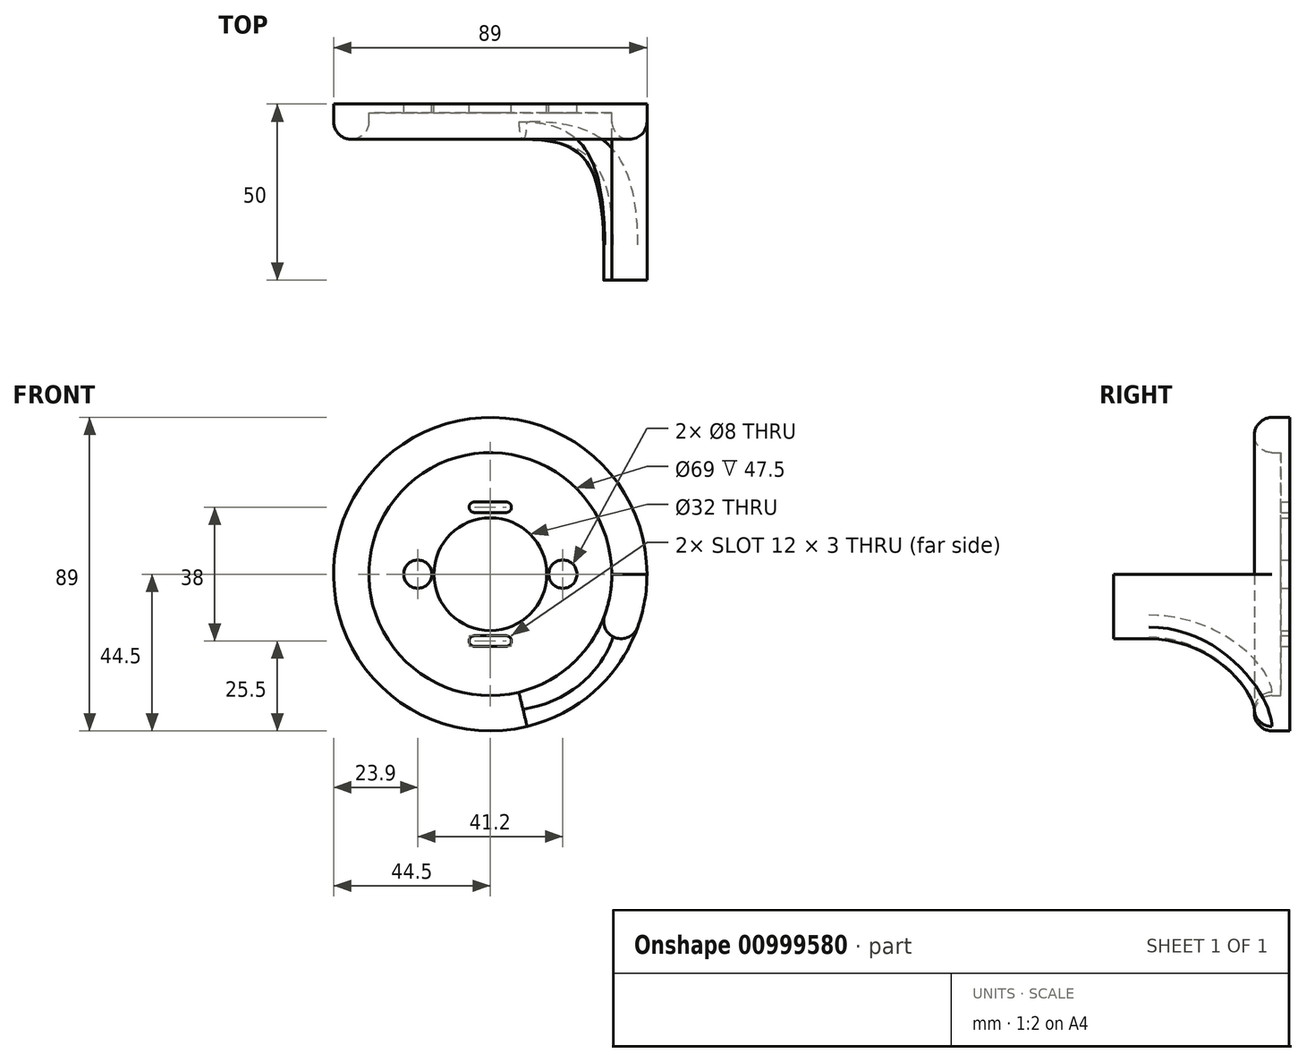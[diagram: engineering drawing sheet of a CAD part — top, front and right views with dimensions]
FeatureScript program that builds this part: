
annotation { "Feature Type Name" : "Feature", "Feature Type Description" : "" }
export const myFeature = defineFeature(function(context is Context, id is Id, definition is map)
    precondition{}
    {
        {
            var Q0;
            Q0=qCreatedBy(makeId("Front.planeOp"),FACE);
            var sketch = newSketch(context, id + "F0", { "sketchPlane" : qUnion([Q0])});
            skCircle(sketch, "E0", {"center": v(0, 0) * mm, "radius": 34.5 * mm});
            skCircle(sketch, "E1", {"center": v(0, 0) * mm, "radius": 44.5 * mm});
            skLineSegment(sketch, "E2", {"start": v(30.74, -15.66) * mm, "end": v(39.65, -20.2) * mm});
            skLineSegment(sketch, "E3", {"start": v(34.5, 0) * mm, "end": v(44.5, 0) * mm});
            skCircle(sketch, "E4", {"center": v(-20.6, 0) * mm, "radius": 4 * mm});
            skCircle(sketch, "E5.MirrorC", {"center": v(20.6, 0) * mm, "radius": 4 * mm});
            skCircle(sketch, "E6", {"center": v(0, 0) * mm, "radius": 16 * mm});
            skArc(sketch, "E7", {"start": v(4.5, 17.5) * mm, "mid": v(6, 19) * mm, "end": v(4.5, 20.5) * mm});
            skLineSegment(sketch, "E8", {"start": v(4.5, 20.5) * mm, "end": v(0, 20.5) * mm});
            skLineSegment(sketch, "E9", {"start": v(4.5, 17.5) * mm, "end": v(0, 17.5) * mm});
            skLineSegment(sketch, "E10.MirrorCS", {"start": v(-4.5, 17.5) * mm, "end": v(0, 17.5) * mm});
            skArc(sketch, "E11.MirrorCS", {"start": v(-4.5, 17.5) * mm, "mid": v(-6, 19) * mm, "end": v(-4.5, 20.5) * mm});
            skLineSegment(sketch, "E12.MirrorCS", {"start": v(-4.5, 20.5) * mm, "end": v(0, 20.5) * mm});
            skLineSegment(sketch, "E13.MirrorCS", {"start": v(-4.5, -17.5) * mm, "end": v(0, -17.5) * mm});
            skArc(sketch, "E14.MirrorCS", {"start": v(4.5, -17.5) * mm, "mid": v(6, -19) * mm, "end": v(4.5, -20.5) * mm});
            skArc(sketch, "E15.MirrorCS", {"start": v(-4.5, -17.5) * mm, "mid": v(-6, -19) * mm, "end": v(-4.5, -20.5) * mm});
            skLineSegment(sketch, "E16.MirrorCS", {"start": v(4.5, -17.5) * mm, "end": v(0, -17.5) * mm});
            skLineSegment(sketch, "E17.MirrorCS", {"start": v(-4.5, -20.5) * mm, "end": v(0, -20.5) * mm});
            skLineSegment(sketch, "E18.MirrorCS", {"start": v(4.5, -20.5) * mm, "end": v(0, -20.5) * mm});
            skSolve(sketch);
        }
        {
            var Q0;
            Q0=makeQuery(id+"F0.imprint","IMPRINT",FACE,{"disambiguationData":[TD([[makeQuery(id+"F0.imprint","IMPRINT",EDGE,{"derivedFrom":sQuery(id+"F0.wireOp",EDGE,"E0")}),-1.0]])]});
            extrude(context, id + "F1", {"entities" : qUnion([Q0]), "depth" : 10 * mm, "offsetDistance" : 25 * mm});
        }
        {
            var Q0;
            {var subQ0=sQuery(id+"F0.wireOp",EDGE,"E2");Q0=makeQuery(id+"F0.imprint","IMPRINT",FACE,{"disambiguationData":[TD([[makeQuery(id+"F0.imprint","IMPRINT",EDGE,{"derivedFrom":subQ0}),1.0]])]});}
            extrude(context, id + "F2", {"entities" : qUnion([Q0]), "operationType" : NewBodyOperationType.ADD, "depth" : 50 * mm, "offsetDistance" : 25 * mm});
        }
        {
            var Q0;
            Q0=makeQuery(id+"F2.boolean.opBoolean","INTERSECT",EDGE,{"derivedFrom":[makeQuery(id+"F1.opExtrude","CAP_FACE",FACE,{"disambiguationData":[OSD([sQuery(id+"F0.wireOp",EDGE,"E0"),sQuery(id+"F0.wireOp",EDGE,"E1")])],"isStart":false}),makeQuery(id+"F2.opExtrude","SWEPT_FACE",FACE,{"disambiguationData":[OSD([sQuery(id+"F0.wireOp",EDGE,"E2")])]})]});
            fillet(context, id + "F3", {"entities" : qUnion([Q0]), "radius" : 30 * mm, "tangentPropagation" : true, "allowEdgeOverflow" : false});
        }
        {
            var Q0;
            {var subQ0=sQuery(id+"F0.wireOp",EDGE,"E0");var subQ1=makeQuery(id+"F0.imprint","INTERSECT",VERTEX,{"derivedFrom":[subQ0,sQuery(id+"F0.wireOp",EDGE,"E2")]});Q0=makeQuery(id+"F0.imprint","IMPRINT",FACE,{"disambiguationData":[TD([[makeQuery(id+"F0.imprint","IMPRINT",EDGE,{"disambiguationData":[TD([[subQ1,1.0]])],"derivedFrom":subQ0}),1.0]])]});}
            extrude(context, id + "F4", {"entities" : qUnion([Q0]), "operationType" : NewBodyOperationType.ADD, "depth" : 2.5 * mm, "offsetDistance" : 25 * mm});
        }
        {
            var Q0;
            Q0=makeQuery(id+"F1.opExtrude","CAP_EDGE",EDGE,{"disambiguationData":[OSD([sQuery(id+"F0.wireOp",EDGE,"E0")])],"isStart":false});
            var Q1;
            Q1=makeQuery(id+"F1.opExtrude","CAP_EDGE",EDGE,{"disambiguationData":[OSD([sQuery(id+"F0.wireOp",EDGE,"E1")])],"isStart":false});
            fillet(context, id + "F5", {"entities" : qUnion([Q0, Q1]), "radius" : 5 * mm, "tangentPropagation" : true, "allowEdgeOverflow" : false});
        }
    });
